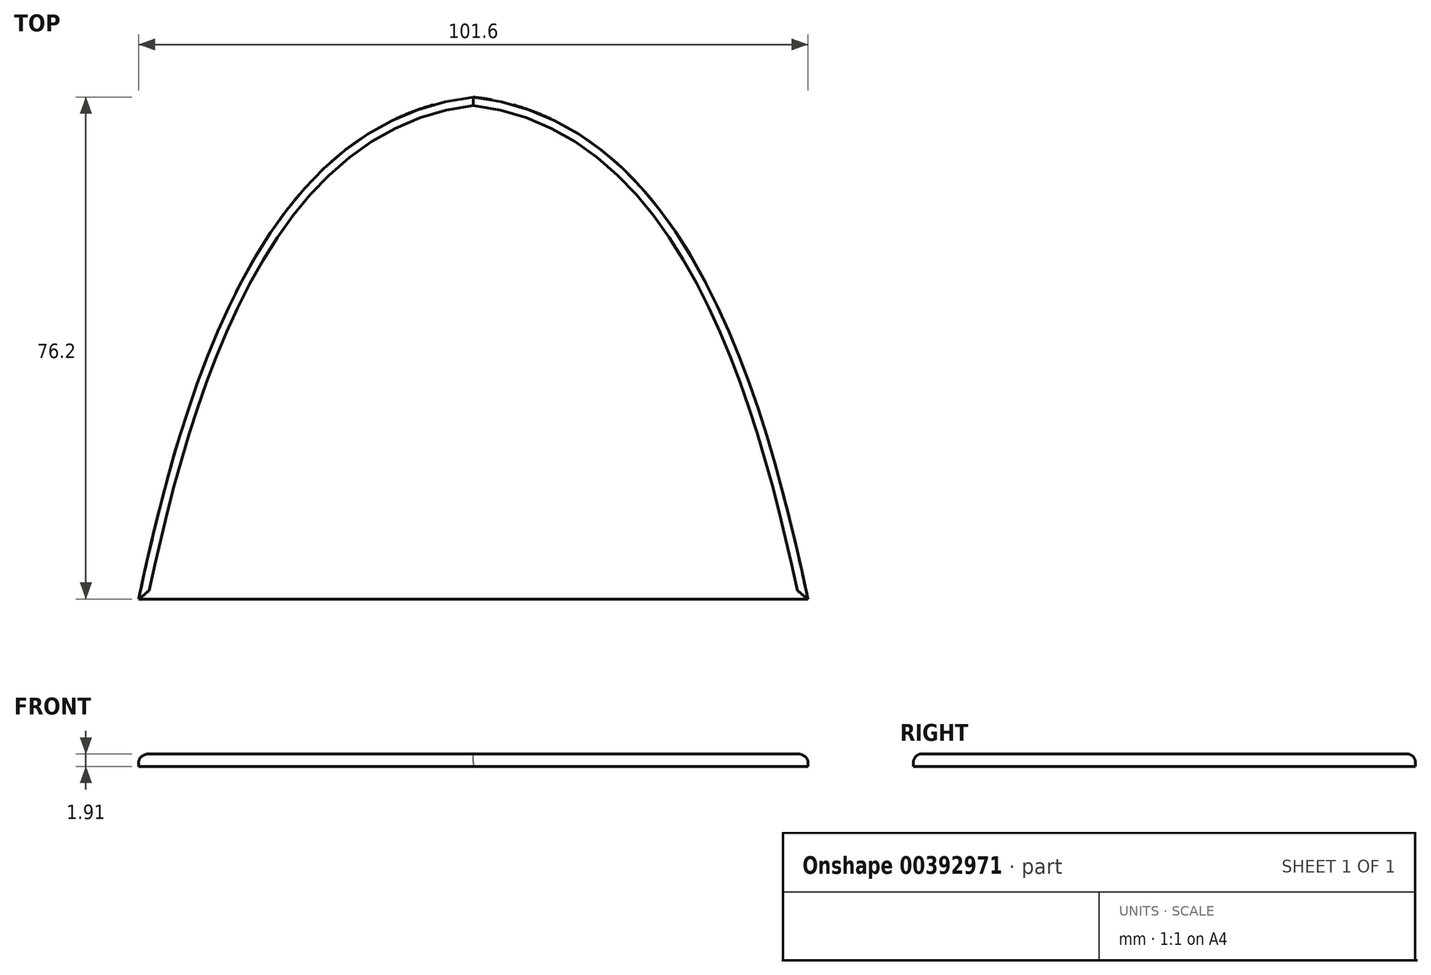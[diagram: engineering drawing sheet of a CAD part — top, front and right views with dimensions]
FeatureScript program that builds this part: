
annotation { "Feature Type Name" : "Feature", "Feature Type Description" : "" }
export const myFeature = defineFeature(function(context is Context, id is Id, definition is map)
    precondition{}
    {
        {
            var Q0;
            Q0=qCreatedBy(makeId("Top.planeOp"),FACE);
            var sketch = newSketch(context, id + "F0", { "sketchPlane" : qUnion([Q0])});
            skLineSegment(sketch, "E0", {"start": v(-50.8, 0) * mm, "end": v(50.8, 0) * mm});
            skFitSpline(sketch, "E1", {"points": [v(-50.8, 0) * mm, v(0, 76.2) * mm], "startDerivative": vector(18.65, 86.3) * mm, "endDerivative": vector(99.9, 11.1) * mm});
            skFitSpline(sketch, "E2.MirrorCS", {"points": [v(50.8, 0) * mm, v(0, 76.2) * mm], "startDerivative": vector(-18.65, 86.3) * mm, "endDerivative": vector(-99.9, 11.1) * mm});
            skFitSpline(sketch, "E3.0", {"points": [v(-44.6, -1.34) * mm, v(-43.82, 2.22) * mm, v(-42.14, 9.77) * mm, v(-38.97, 21.7) * mm, v(-35, 33.62) * mm, v(-30.1, 44.81) * mm, v(-25.13, 52.98) * mm, v(-20.63, 58.5) * mm, v(-17, 62.09) * mm, v(-13.1, 65.05) * mm, v(-8.9, 67.38) * mm, v(-4.37, 69.05) * mm, v(-1.05, 69.7) * mm, v(0.7, 69.89) * mm]});
            skLineSegment(sketch, "E4", {"start": v(0, 0) * mm, "end": v(0, 76.2) * mm, "construction": true});
            skLineSegment(sketch, "E5", {"start": v(-37.7, 25.4) * mm, "end": v(0, 25.4) * mm});
            skLineSegment(sketch, "E6.MirrorCS", {"start": v(0, 50.8) * mm, "end": v(0, -25.4) * mm, "construction": true});
            skFitSpline(sketch, "E7.0", {"points": [v(44.6, -1.34) * mm, v(43.82, 2.22) * mm, v(42.14, 9.77) * mm, v(38.97, 21.7) * mm, v(35, 33.62) * mm, v(30.1, 44.81) * mm, v(25.13, 52.98) * mm, v(20.63, 58.5) * mm, v(17, 62.09) * mm, v(13.1, 65.05) * mm, v(8.9, 67.38) * mm, v(4.37, 69.05) * mm, v(1.05, 69.7) * mm, v(-0.7, 69.89) * mm]});
            skLineSegment(sketch, "E8", {"start": v(0, 25.4) * mm, "end": v(37.7, 25.4) * mm});
            skSolve(sketch);
        }
        {
            var Q0;
            Q0=qSketchRegion(id+"F0",true);
            extrude(context, id + "F1", {"entities" : qUnion([Q0]), "depth" : 1.9 * mm});
        }
        {
            var Q0;
            Q0=makeQuery(id+"F1.opExtrude","CAP_FACE",FACE,{"disambiguationData":[OSD([sQuery(id+"F0.wireOp",EDGE,"E0"),sQuery(id+"F0.wireOp",EDGE,"E1"),sQuery(id+"F0.wireOp",EDGE,"E2.MirrorCS")])],"isStart":false});
            fillet(context, id + "F2", {"entities" : qUnion([Q0]), "radius" : 1.27 * mm, "tangentPropagation" : true, "allowEdgeOverflow" : false});
        }
    });
